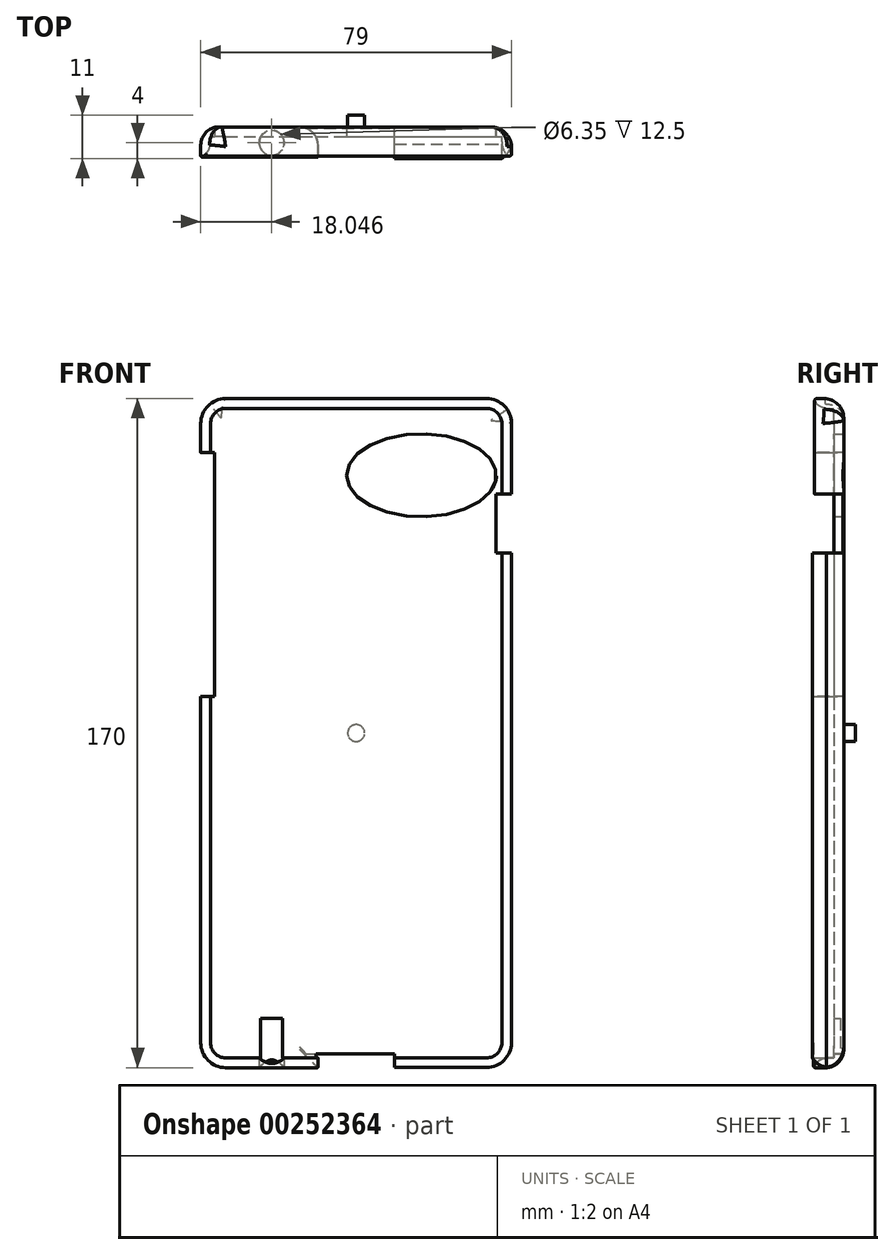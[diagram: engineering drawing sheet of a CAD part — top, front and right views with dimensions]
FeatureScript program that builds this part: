
annotation { "Feature Type Name" : "Feature", "Feature Type Description" : "" }
export const myFeature = defineFeature(function(context is Context, id is Id, definition is map)
    precondition{}
    {
        {
            var Q0;
            Q0=qCreatedBy(makeId("Front.planeOp"),FACE);
            var sketch = newSketch(context, id + "F0", { "sketchPlane" : qUnion([Q0])});
            skLineSegment(sketch, "E0.bottom", {"start": v(-39.5, 85) * mm, "end": v(39.5, 85) * mm});
            skLineSegment(sketch, "E0.top", {"start": v(-39.5, -85) * mm, "end": v(39.5, -85) * mm});
            skLineSegment(sketch, "E0.left", {"start": v(-39.5, 85) * mm, "end": v(-39.5, -85) * mm});
            skLineSegment(sketch, "E0.right", {"start": v(39.5, 85) * mm, "end": v(39.5, -85) * mm});
            skPoint(sketch, "E0.middle", {"position": v(0, 0) * mm});
            skSolve(sketch);
        }
        {
            var Q0;
            Q0=makeQuery(id+"F0.imprint","IMPRINT",FACE,{"disambiguationData":[TD([[makeQuery(id+"F0.imprint","IMPRINT",EDGE,{"derivedFrom":sQuery(id+"F0.wireOp",EDGE,"E0.bottom")}),-1.0]])]});
            extrude(context, id + "F1", {"entities" : qUnion([Q0]), "endBound" : BoundingType.SYMMETRIC, "depth" : 8 * mm});
        }
        {
            var Q0;
            Q0=makeQuery(id+"F1.opExtrude","SWEPT_EDGE",EDGE,{"disambiguationData":[OSD([sQuery(id+"F0.wireOp",EDGE,"E0.bottom"),sQuery(id+"F0.wireOp",EDGE,"E0.left")])]});
            var Q1;
            Q1=makeQuery(id+"F1.opExtrude","SWEPT_EDGE",EDGE,{"disambiguationData":[OSD([sQuery(id+"F0.wireOp",EDGE,"E0.bottom"),sQuery(id+"F0.wireOp",EDGE,"E0.right")])]});
            var Q2;
            Q2=makeQuery(id+"F1.opExtrude","SWEPT_EDGE",EDGE,{"disambiguationData":[OSD([sQuery(id+"F0.wireOp",EDGE,"E0.top"),sQuery(id+"F0.wireOp",EDGE,"E0.right")])]});
            var Q3;
            Q3=makeQuery(id+"F1.opExtrude","SWEPT_EDGE",EDGE,{"disambiguationData":[OSD([sQuery(id+"F0.wireOp",EDGE,"E0.top"),sQuery(id+"F0.wireOp",EDGE,"E0.left")])]});
            fillet(context, id + "F2", {"entities" : qUnion([Q0, Q1, Q2, Q3]), "radius" : 6.35 * mm, "tangentPropagation" : true, "allowEdgeOverflow" : false});
        }
        {
            var Q0;
            Q0=makeQuery(id+"F1.opExtrude","CAP_FACE",FACE,{"disambiguationData":[OSD([sQuery(id+"F0.wireOp",EDGE,"E0.bottom"),sQuery(id+"F0.wireOp",EDGE,"E0.top"),sQuery(id+"F0.wireOp",EDGE,"E0.left"),sQuery(id+"F0.wireOp",EDGE,"E0.right")])],"isStart":false});
            shell(context, id + "F3", {"entities" : qUnion([Q0]), "thickness" : 2.5 * mm});
        }
        {
            var Q0;
            Q0=makeQuery(id+"F1.opExtrude","SWEPT_FACE",FACE,{"disambiguationData":[OSD([sQuery(id+"F0.wireOp",EDGE,"E0.top")])]});
            var sketch = newSketch(context, id + "F4", { "sketchPlane" : qUnion([Q0])});
            skLineSegment(sketch, "E1.bottom", {"start": v(-9.76, 4) * mm, "end": v(9.76, 4) * mm});
            skLineSegment(sketch, "E1.top", {"start": v(-9.76, -4) * mm, "end": v(9.76, -4) * mm});
            skLineSegment(sketch, "E1.left", {"start": v(-9.76, 4) * mm, "end": v(-9.76, -4) * mm});
            skLineSegment(sketch, "E1.right", {"start": v(9.76, 4) * mm, "end": v(9.76, -4) * mm});
            skPoint(sketch, "E1.middle", {"position": v(0, 0) * mm});
            skSolve(sketch);
        }
        {
            var Q0;
            Q0 = qSketchRegion(id + "F4", true);
            extrude(context, id + "F5", {"entities" : qUnion([Q0]), "operationType" : NewBodyOperationType.REMOVE, "endBound" : BoundingType.SYMMETRIC, "depth" : 7.1 * mm});
        }
        {
            var Q0;
            Q0=makeQuery(id+"F1.opExtrude","SWEPT_FACE",FACE,{"disambiguationData":[OSD([sQuery(id+"F0.wireOp",EDGE,"E0.right")])]});
            var sketch = newSketch(context, id + "F6", { "sketchPlane" : qUnion([Q0])});
            skLineSegment(sketch, "E2.bottom", {"start": v(-4, 60.7) * mm, "end": v(4, 60.7) * mm});
            skLineSegment(sketch, "E2.top", {"start": v(-4, 45.74) * mm, "end": v(4, 45.74) * mm});
            skLineSegment(sketch, "E2.left", {"start": v(-4, 60.7) * mm, "end": v(-4, 45.74) * mm});
            skLineSegment(sketch, "E2.right", {"start": v(4, 60.7) * mm, "end": v(4, 45.74) * mm});
            skPoint(sketch, "E2.middle", {"position": v(0, 53.22) * mm});
            skSolve(sketch);
        }
        {
            var Q0;
            Q0=makeQuery(id+"F6.imprint","IMPRINT",FACE,{"disambiguationData":[TD([[makeQuery(id+"F6.imprint","IMPRINT",EDGE,{"derivedFrom":sQuery(id+"F6.wireOp",EDGE,"E2.bottom")}),-1.0]])]});
            extrude(context, id + "F7", {"entities" : qUnion([Q0]), "operationType" : NewBodyOperationType.REMOVE, "endBound" : BoundingType.SYMMETRIC, "oppositeDirection" : true, "depth" : 8 * mm});
        }
        {
            var Q0;
            Q0=makeQuery(id+"F1.opExtrude","SWEPT_FACE",FACE,{"disambiguationData":[OSD([sQuery(id+"F0.wireOp",EDGE,"E0.left")])]});
            var sketch = newSketch(context, id + "F8", { "sketchPlane" : qUnion([Q0])});
            skLineSegment(sketch, "E3.bottom", {"start": v(-4, 71.24) * mm, "end": v(4, 71.24) * mm});
            skLineSegment(sketch, "E3.top", {"start": v(-4, 9.35) * mm, "end": v(4, 9.35) * mm});
            skLineSegment(sketch, "E3.left", {"start": v(-4, 71.24) * mm, "end": v(-4, 9.35) * mm});
            skLineSegment(sketch, "E3.right", {"start": v(4, 71.24) * mm, "end": v(4, 9.35) * mm});
            skPoint(sketch, "E3.middle", {"position": v(0, 40.3) * mm});
            skSolve(sketch);
        }
        {
            var Q0;
            Q0=makeQuery(id+"F8.imprint","IMPRINT",FACE,{"disambiguationData":[TD([[makeQuery(id+"F8.imprint","IMPRINT",EDGE,{"derivedFrom":sQuery(id+"F8.wireOp",EDGE,"E3.bottom")}),-1.0]])]});
            extrude(context, id + "F9", {"entities" : qUnion([Q0]), "operationType" : NewBodyOperationType.REMOVE, "endBound" : BoundingType.SYMMETRIC, "oppositeDirection" : true, "depth" : 7 * mm});
        }
        {
            var Q0;
            Q0=makeQuery(id+"F1.opExtrude","CAP_FACE",FACE,{"disambiguationData":[OSD([sQuery(id+"F0.wireOp",EDGE,"E0.bottom"),sQuery(id+"F0.wireOp",EDGE,"E0.top"),sQuery(id+"F0.wireOp",EDGE,"E0.left"),sQuery(id+"F0.wireOp",EDGE,"E0.right")])],"isStart":true});
            var sketch = newSketch(context, id + "F10", { "sketchPlane" : qUnion([Q0])});
            skPoint(sketch, "E4.centerSnap0", {"position": v(-39.5, 69.67) * mm});
            skEllipse(sketch, "E5", {"center": v(-16.6, 65.5) * mm, "majorRadius": 19.03 * mm, "minorRadius": 10.53 * mm, "majorAxis": v(1, 0)});
            skSolve(sketch);
        }
        {
            var Q0;
            Q0=makeQuery(id+"F10.imprint","IMPRINT",FACE,{"disambiguationData":[TD([[makeQuery(id+"F10.imprint","IMPRINT",EDGE,{"derivedFrom":sQuery(id+"F10.wireOp",EDGE,"E5")}),1.0]])]});
            extrude(context, id + "F11", {"entities" : qUnion([Q0]), "operationType" : NewBodyOperationType.REMOVE, "endBound" : BoundingType.SYMMETRIC, "depth" : 25 * mm});
        }
        {
            var Q0;
            {var subQ2=sQuery(id+"F0.wireOp",EDGE,"E0.top");Q0=makeQuery(id+"F5.boolean.opBoolean","SPLIT",FACE,{"disambiguationData":[TD([makeQuery(id+"F5.opExtrude","SWEPT_FACE",FACE,{"disambiguationData":[OSD([sQuery(id+"F4.wireOp",EDGE,"E1.left")])]})])],"derivedFrom":makeQuery(id+"F1.opExtrude","SWEPT_FACE",FACE,{"disambiguationData":[OSD([subQ2])]})});}
            var sketch = newSketch(context, id + "F12", { "sketchPlane" : qUnion([Q0])});
            skCircle(sketch, "E6", {"center": v(-21.45, 0) * mm, "radius": 3.18 * mm});
            skPoint(sketch, "E6.centerSnap0", {"position": v(-21.45, 4) * mm});
            skSolve(sketch);
        }
        {
            var Q0;
            Q0=makeQuery(id+"F12.imprint","IMPRINT",FACE,{"disambiguationData":[TD([[makeQuery(id+"F12.imprint","IMPRINT",EDGE,{"derivedFrom":sQuery(id+"F12.wireOp",EDGE,"E6")}),1.0]])]});
            extrude(context, id + "F13", {"entities" : qUnion([Q0]), "operationType" : NewBodyOperationType.REMOVE, "endBound" : BoundingType.SYMMETRIC, "oppositeDirection" : true, "depth" : 25 * mm});
        }
        {
            var Q0;
            {var subQ0=sQuery(id+"F0.wireOp",EDGE,"E0.right");Q0=makeQuery(id+"F7.boolean.opBoolean","SPLIT",EDGE,{"disambiguationData":[TD([makeQuery(id+"F7.opExtrude","SWEPT_FACE",FACE,{"disambiguationData":[OSD([sQuery(id+"F6.wireOp",EDGE,"E2.top")])]})])],"derivedFrom":makeQuery(id+"F1.opExtrude","CAP_EDGE",EDGE,{"disambiguationData":[OSD([subQ0])],"isStart":true})});}
            var Q1;
            {var subQ0=sQuery(id+"F0.wireOp",EDGE,"E0.right");Q1=makeQuery(id+"F7.boolean.opBoolean","SPLIT",EDGE,{"disambiguationData":[TD([makeQuery(id+"F7.opExtrude","SWEPT_FACE",FACE,{"disambiguationData":[OSD([sQuery(id+"F6.wireOp",EDGE,"E2.top")])]})])],"derivedFrom":makeQuery(id+"F1.opExtrude","CAP_EDGE",EDGE,{"disambiguationData":[OSD([subQ0])],"isStart":false})});}
            fillet(context, id + "F14", {"entities" : qUnion([Q0, Q1]), "radius" : 5.24 * mm, "tangentPropagation" : true, "allowEdgeOverflow" : false});
        }
        {
            var Q0;
            {var subQ0=sQuery(id+"F0.wireOp",EDGE,"E0.right");var subQ1=sQuery(id+"F0.wireOp",EDGE,"E0.left");var subQ2=sQuery(id+"F0.wireOp",EDGE,"E0.top");var subQ3=sQuery(id+"F0.wireOp",EDGE,"E0.bottom");Q0=makeQuery(id+"F3.opShell","OFFSET_EDGE",EDGE,{"disambiguationData":[OSD([subQ3,subQ2,subQ1,subQ0]),TDD([makeQuery(id+"F2.opFillet","BLEND_EDGE",EDGE,{"blendedFrom":[makeQuery(id+"F1.opExtrude","SWEPT_EDGE",EDGE,{"disambiguationData":[OSD([subQ3,subQ0])]}),makeQuery(id+"F1.opExtrude","CAP_FACE",FACE,{"disambiguationData":[OSD([subQ3,subQ2,subQ1,subQ0])],"isStart":false})],"blendedInto":[makeQuery(id+"F1.opExtrude","CAP_FACE",FACE,{"disambiguationData":[OSD([subQ3,subQ2,subQ1,subQ0])],"isStart":false})]})])]});}
            var Q1;
            {var subQ0=sQuery(id+"F0.wireOp",EDGE,"E0.right");Q1=makeQuery(id+"F7.boolean.opBoolean","SPLIT",EDGE,{"disambiguationData":[TD([makeQuery(id+"F7.opExtrude","SWEPT_FACE",FACE,{"disambiguationData":[OSD([sQuery(id+"F6.wireOp",EDGE,"E2.bottom")])]})])],"derivedFrom":makeQuery(id+"F3.opShell","OFFSET_EDGE",EDGE,{"disambiguationData":[OSD([subQ0]),TDD([makeQuery(id+"F1.opExtrude","CAP_EDGE",EDGE,{"disambiguationData":[OSD([subQ0])],"isStart":false})])]})});}
            var Q2;
            {var subQ0=sQuery(id+"F0.wireOp",EDGE,"E0.right");var subQ1=sQuery(id+"F0.wireOp",EDGE,"E0.left");var subQ2=sQuery(id+"F0.wireOp",EDGE,"E0.top");var subQ3=sQuery(id+"F0.wireOp",EDGE,"E0.bottom");Q2=makeQuery(id+"F3.opShell","OFFSET_EDGE",EDGE,{"disambiguationData":[OSD([subQ3,subQ2,subQ1,subQ0]),TDD([makeQuery(id+"F2.opFillet","BLEND_EDGE",EDGE,{"blendedFrom":[makeQuery(id+"F1.opExtrude","SWEPT_EDGE",EDGE,{"disambiguationData":[OSD([subQ3,subQ1])]}),makeQuery(id+"F1.opExtrude","CAP_FACE",FACE,{"disambiguationData":[OSD([subQ3,subQ2,subQ1,subQ0])],"isStart":false})],"blendedInto":[makeQuery(id+"F1.opExtrude","CAP_FACE",FACE,{"disambiguationData":[OSD([subQ3,subQ2,subQ1,subQ0])],"isStart":false})]})])]});}
            var Q3;
            {var subQ0=sQuery(id+"F0.wireOp",EDGE,"E0.left");Q3=makeQuery(id+"F9.boolean.opBoolean","SPLIT",EDGE,{"disambiguationData":[TD([makeQuery(id+"F9.opExtrude","SWEPT_FACE",FACE,{"disambiguationData":[OSD([sQuery(id+"F8.wireOp",EDGE,"E3.top")])]})])],"derivedFrom":makeQuery(id+"F3.opShell","OFFSET_EDGE",EDGE,{"disambiguationData":[OSD([subQ0]),TDD([makeQuery(id+"F1.opExtrude","CAP_EDGE",EDGE,{"disambiguationData":[OSD([subQ0])],"isStart":false})])]})});}
            var Q4;
            {var subQ0=sQuery(id+"F0.wireOp",EDGE,"E0.left");Q4=makeQuery(id+"F9.boolean.opBoolean","SPLIT",EDGE,{"disambiguationData":[TD([makeQuery(id+"F9.opExtrude","SWEPT_FACE",FACE,{"disambiguationData":[OSD([sQuery(id+"F8.wireOp",EDGE,"E3.bottom")])]})])],"derivedFrom":makeQuery(id+"F3.opShell","OFFSET_EDGE",EDGE,{"disambiguationData":[OSD([subQ0]),TDD([makeQuery(id+"F1.opExtrude","CAP_EDGE",EDGE,{"disambiguationData":[OSD([subQ0])],"isStart":false})])]})});}
            var Q5;
            {var subQ0=sQuery(id+"F0.wireOp",EDGE,"E0.right");var subQ1=sQuery(id+"F0.wireOp",EDGE,"E0.left");var subQ2=sQuery(id+"F0.wireOp",EDGE,"E0.top");var subQ3=sQuery(id+"F0.wireOp",EDGE,"E0.bottom");Q5=makeQuery(id+"F3.opShell","OFFSET_EDGE",EDGE,{"disambiguationData":[OSD([subQ3,subQ2,subQ1,subQ0]),TDD([makeQuery(id+"F2.opFillet","BLEND_EDGE",EDGE,{"blendedFrom":[makeQuery(id+"F1.opExtrude","SWEPT_EDGE",EDGE,{"disambiguationData":[OSD([subQ2,subQ1])]}),makeQuery(id+"F1.opExtrude","CAP_FACE",FACE,{"disambiguationData":[OSD([subQ3,subQ2,subQ1,subQ0])],"isStart":false})],"blendedInto":[makeQuery(id+"F1.opExtrude","CAP_FACE",FACE,{"disambiguationData":[OSD([subQ3,subQ2,subQ1,subQ0])],"isStart":false})]})])]});}
            fillet(context, id + "F15", {"entities" : qUnion([Q0, Q1, Q2, Q3, Q4, Q5]), "radius" : 5 * mm, "tangentPropagation" : true, "allowEdgeOverflow" : false});
        }
        {
            var Q0;
            Q0=makeQuery(id+"F5.boolean.opBoolean","INTERSECT",EDGE,{"derivedFrom":[makeQuery(id+"F1.opExtrude","SWEPT_FACE",FACE,{"disambiguationData":[OSD([sQuery(id+"F0.wireOp",EDGE,"E0.top")])]}),makeQuery(id+"F5.opExtrude","SWEPT_FACE",FACE,{"disambiguationData":[OSD([sQuery(id+"F4.wireOp",EDGE,"E1.left")])]})]});
            var Q1;
            {var subQ0=makeQuery(id+"F5.opExtrude","SWEPT_FACE",FACE,{"disambiguationData":[OSD([sQuery(id+"F4.wireOp",EDGE,"E1.left")])]});var subQ2=sQuery(id+"F0.wireOp",EDGE,"E0.top");Q1=makeQuery(id+"F15.opFillet","BLEND_EDGE",EDGE,{"blendedFrom":[makeQuery(id+"F5.boolean.opBoolean","SPLIT",EDGE,{"disambiguationData":[TD([subQ0])],"derivedFrom":makeQuery(id+"F3.opShell","OFFSET_EDGE",EDGE,{"disambiguationData":[OSD([subQ2]),TDD([makeQuery(id+"F1.opExtrude","CAP_EDGE",EDGE,{"disambiguationData":[OSD([subQ2])],"isStart":false})])]})}),makeQuery(id+"F5.boolean.opBoolean","COPY",FACE,{"derivedFrom":subQ0})],"blendedInto":[makeQuery(id+"F5.boolean.opBoolean","COPY",FACE,{"derivedFrom":subQ0})]});}
            var Q2;
            Q2=makeQuery(id+"F5.boolean.opBoolean","COPY",EDGE,{"derivedFrom":makeQuery(id+"F5.opExtrude","SWEPT_EDGE",EDGE,{"disambiguationData":[OSD([sQuery(id+"F0.wireOp",EDGE,"E0.top"),sQuery(id+"F4.wireOp",EDGE,"E1.top"),sQuery(id+"F4.wireOp",EDGE,"E1.left")])]})});
            fillet(context, id + "F16", {"entities" : qUnion([Q0, Q1, Q2]), "radius" : 0.02 * mm, "tangentPropagation" : true, "allowEdgeOverflow" : false});
        }
        {
            var Q0;
            {var subQ1=sQuery(id+"F0.wireOp",EDGE,"E0.top");Q0=makeQuery(id+"F5.boolean.opBoolean","SPLIT",EDGE,{"disambiguationData":[TD([makeQuery(id+"F5.opExtrude","SWEPT_FACE",FACE,{"disambiguationData":[OSD([sQuery(id+"F4.wireOp",EDGE,"E1.left")])]})])],"derivedFrom":makeQuery(id+"F1.opExtrude","CAP_EDGE",EDGE,{"disambiguationData":[OSD([subQ1])],"isStart":true})});}
            fillet(context, id + "F17", {"entities" : qUnion([Q0]), "radius" : 4.6 * mm, "tangentPropagation" : true, "allowEdgeOverflow" : false});
        }
        {
            var Q0;
            {var subQ2=sQuery(id+"F0.wireOp",EDGE,"E0.top");var subQ5=makeQuery(id+"F5.opExtrude","SWEPT_FACE",FACE,{"disambiguationData":[OSD([sQuery(id+"F4.wireOp",EDGE,"E1.left")])]});Q0=makeQuery(id+"F15.opFillet","BLEND_EDGE",EDGE,{"blendedFrom":[makeQuery(id+"F5.boolean.opBoolean","SPLIT",EDGE,{"disambiguationData":[TD([subQ5])],"derivedFrom":makeQuery(id+"F3.opShell","OFFSET_EDGE",EDGE,{"disambiguationData":[OSD([subQ2]),TDD([makeQuery(id+"F1.opExtrude","CAP_EDGE",EDGE,{"disambiguationData":[OSD([subQ2])],"isStart":false})])]})}),makeQuery(id+"F5.boolean.opBoolean","SPLIT",FACE,{"disambiguationData":[TD([subQ5])],"derivedFrom":makeQuery(id+"F1.opExtrude","SWEPT_FACE",FACE,{"disambiguationData":[OSD([subQ2])]})})],"blendedInto":[makeQuery(id+"F5.boolean.opBoolean","SPLIT",FACE,{"disambiguationData":[TD([subQ5])],"derivedFrom":makeQuery(id+"F1.opExtrude","SWEPT_FACE",FACE,{"disambiguationData":[OSD([subQ2])]})})]});}
            fillet(context, id + "F18", {"entities" : qUnion([Q0]), "radius" : .4 * mm, "tangentPropagation" : true, "allowEdgeOverflow" : false});
        }
        {
            var Q0;
            {var subQ0=sQuery(id+"F0.wireOp",EDGE,"E0.bottom");var subQ1=sQuery(id+"F0.wireOp",EDGE,"E0.right");Q0=makeQuery(id+"F15.opFillet","BLEND_EDGE",EDGE,{"blendedFrom":[makeQuery(id+"F7.boolean.opBoolean","SPLIT",EDGE,{"disambiguationData":[TD([makeQuery(id+"F7.opExtrude","SWEPT_FACE",FACE,{"disambiguationData":[OSD([sQuery(id+"F6.wireOp",EDGE,"E2.bottom")])]})])],"derivedFrom":makeQuery(id+"F3.opShell","OFFSET_EDGE",EDGE,{"disambiguationData":[OSD([subQ1]),TDD([makeQuery(id+"F1.opExtrude","CAP_EDGE",EDGE,{"disambiguationData":[OSD([subQ1])],"isStart":false})])]})}),makeQuery(id+"F1.opExtrude","SWEPT_FACE",FACE,{"disambiguationData":[OSD([subQ0])]})],"blendedInto":[makeQuery(id+"F1.opExtrude","SWEPT_FACE",FACE,{"disambiguationData":[OSD([subQ0])]})]});}
            fillet(context, id + "F19", {"entities" : qUnion([Q0]), "radius" : .6 * mm, "tangentPropagation" : true, "allowEdgeOverflow" : false});
        }
        {
            var Q0;
            Q0=makeQuery(id+"F1.opExtrude","CAP_EDGE",EDGE,{"disambiguationData":[OSD([sQuery(id+"F0.wireOp",EDGE,"E0.bottom")])],"isStart":true});
            fillet(context, id + "F20", {"entities" : qUnion([Q0]), "radius" : 5 * mm, "tangentPropagation" : true, "allowEdgeOverflow" : false});
        }
        {
            var Q0;
            Q0=makeQuery(id+"F1.opExtrude","CAP_FACE",FACE,{"disambiguationData":[OSD([sQuery(id+"F0.wireOp",EDGE,"E0.bottom"),sQuery(id+"F0.wireOp",EDGE,"E0.top"),sQuery(id+"F0.wireOp",EDGE,"E0.left"),sQuery(id+"F0.wireOp",EDGE,"E0.right")])],"isStart":true});
            var sketch = newSketch(context, id + "F21", { "sketchPlane" : qUnion([Q0])});
            skCircle(sketch, "E7", {"center": v(0, 0) * mm, "radius": 2.15 * mm});
            skSolve(sketch);
        }
        {
            var Q0;
            Q0=makeQuery(id+"F21.imprint","IMPRINT",FACE,{"disambiguationData":[TD([[makeQuery(id+"F21.imprint","IMPRINT",EDGE,{"derivedFrom":sQuery(id+"F21.wireOp",EDGE,"E7")}),1.0]])]});
            extrude(context, id + "F22", {"entities" : qUnion([Q0]), "operationType" : NewBodyOperationType.ADD, "depth" : 3 * mm});
        }
    });
